# Revit family: Shower-Outlet-Dorf Jovian-Hand1
name_source: partatom
category: Plumbing Fixtures
revit_build: Autodesk Revit 2014 (Build: 20131024_2115(x64)
units: mm (PartAtom-declared; Revit-internal decimal feet)

## types (1)
- Standard
    Assembly Code = D2010710
    CW Connection = Yes
    CWFU = 2.37
    Connector Radius = 10 mm  [stored 0.0328084 ft]
    Default Elevation = 1650 mm  [stored 5.41339 ft]
    Description = Sharp, intense lines. Smooth edges. Distinctively European-looking range to compliment any modern bathroom.
    HW Connection = Yes
    HWFU = 2.37
    Height_ANZRS = 706 mm  [stored 2.31627 ft]
    Keynote = SHR
    Length_ANZRS = 148 mm  [stored 0.485564 ft]
    Manufacturer = GWA Bathrooms & Kitchens
    Material_ANZRS = Metal-Chrome-Caroma
    Model = 2129.043A
    ModifiedIssue_ANZRS = 20150112 $
    Type Comments = Dorf Jovian Hand Shower
    URL = http://specify.caroma.com.au
    Vent Connection = No
    Waste Connection = No
    Width_ANZRS = 65 mm  [stored 0.213255 ft]

note: [stored X ft] marks values corroborated as IEEE doubles in the binary element streams (Revit-internal decimal feet)

## geometry (parser evidence)
native form markers: Blend x12, Sweep x1
no freeform markers — native parametric forms only
